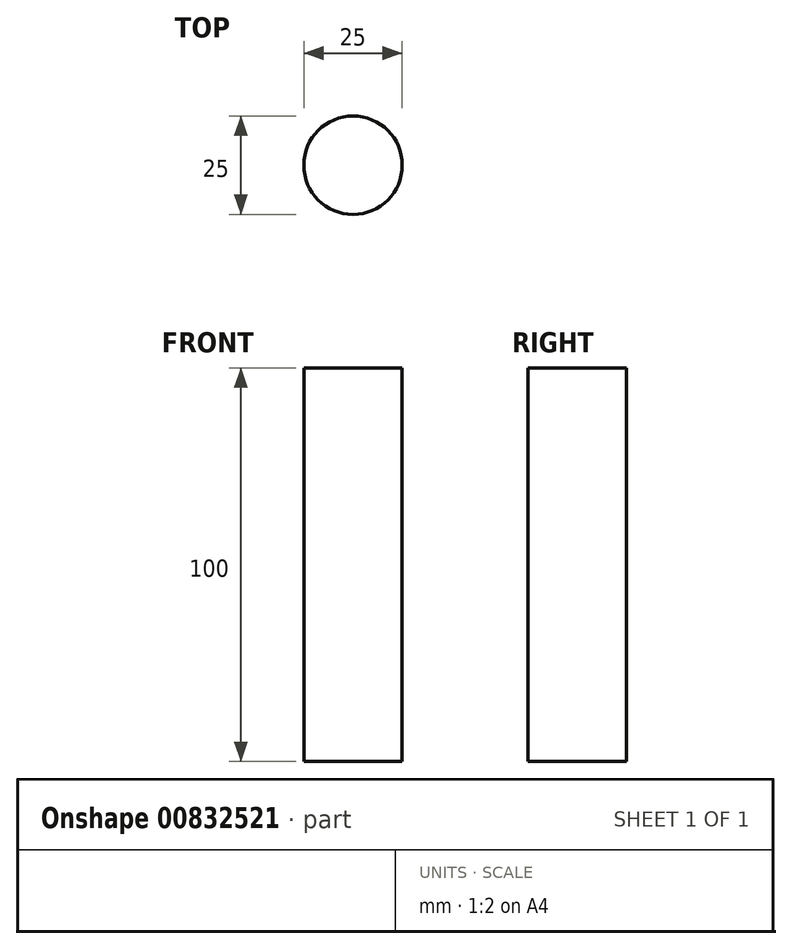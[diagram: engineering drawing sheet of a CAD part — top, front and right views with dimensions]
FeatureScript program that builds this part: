
annotation { "Feature Type Name" : "Feature", "Feature Type Description" : "" }
export const myFeature = defineFeature(function(context is Context, id is Id, definition is map)
    precondition{}
    {
        {
            var Q0;
            Q0=qCreatedBy(makeId("Top.planeOp"),FACE);
            var sketch = newSketch(context, id + "F0", { "sketchPlane" : qUnion([Q0])});
            skCircle(sketch, "E0", {"center": v(0, 0) * mm, "radius": 12.5 * mm});
            skSolve(sketch);
        }
        {
            var Q0;
            Q0=makeQuery(id+"F0.imprint","IMPRINT",FACE,{"disambiguationData":[TD([[makeQuery(id+"F0.imprint","IMPRINT",EDGE,{"derivedFrom":sQuery(id+"F0.wireOp",EDGE,"E0")}),1.0]])]});
            extrude(context, id + "F1", {"entities" : qUnion([Q0]), "depth" : 100 * mm, "offsetDistance" : 25 * mm});
        }
    });
